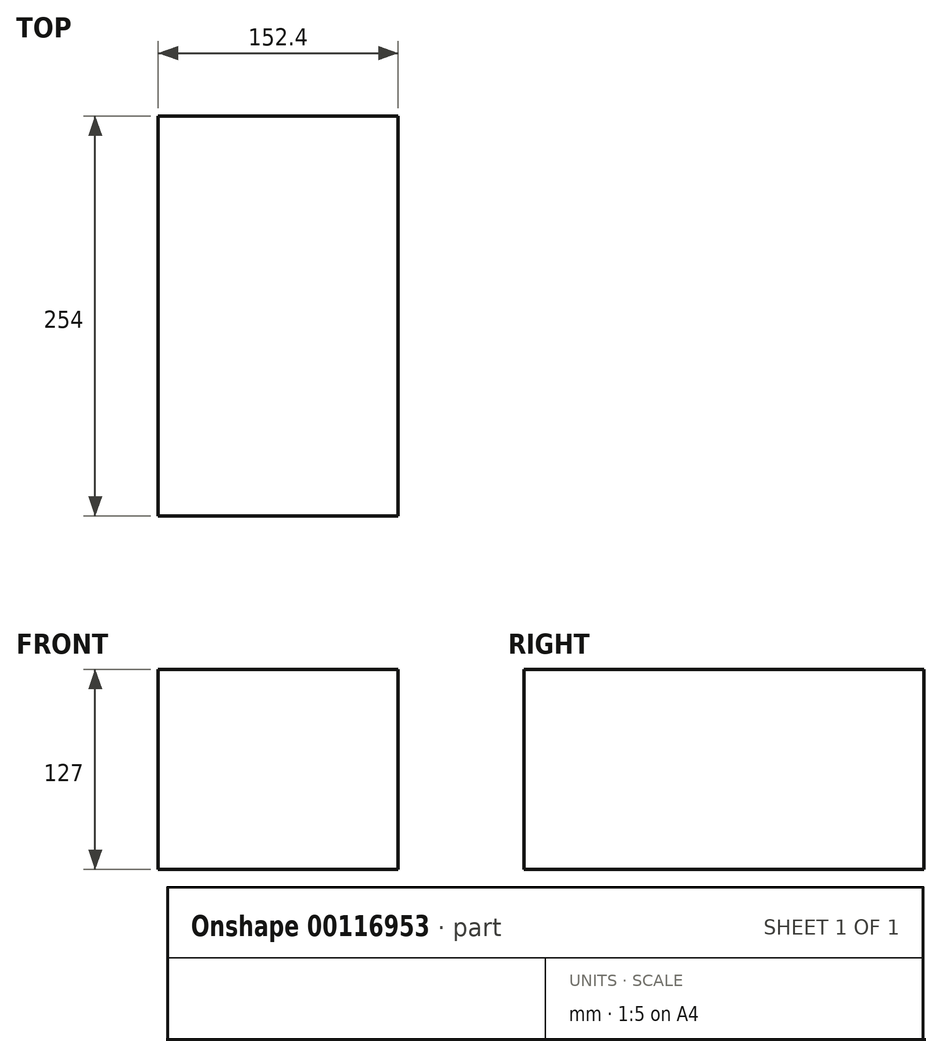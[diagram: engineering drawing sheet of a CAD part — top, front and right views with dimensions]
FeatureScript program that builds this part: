
annotation { "Feature Type Name" : "Feature", "Feature Type Description" : "" }
export const myFeature = defineFeature(function(context is Context, id is Id, definition is map)
    precondition{}
    {
        {
            var Q0;
            Q0=qCreatedBy(makeId("Top.planeOp"),FACE);
            var sketch = newSketch(context, id + "F0", { "sketchPlane" : qUnion([Q0])});
            skLineSegment(sketch, "E0.bottom", {"start": v(-76.2, 127) * mm, "end": v(76.2, 127) * mm});
            skLineSegment(sketch, "E0.top", {"start": v(-76.2, -127) * mm, "end": v(76.2, -127) * mm});
            skLineSegment(sketch, "E0.left", {"start": v(-76.2, 127) * mm, "end": v(-76.2, -127) * mm});
            skLineSegment(sketch, "E0.right", {"start": v(76.2, 127) * mm, "end": v(76.2, -127) * mm});
            skPoint(sketch, "E0.middle", {"position": v(0, 0) * mm});
            skLineSegment(sketch, "E1", {"start": v(0, 0) * mm, "end": v(0, 127) * mm, "construction": true});
            skLineSegment(sketch, "E2", {"start": v(-76.2, 76.2) * mm, "end": v(76.2, 76.2) * mm, "construction": true});
            skLineSegment(sketch, "E3", {"start": v(-63.5, 127) * mm, "end": v(-63.5, 76.2) * mm, "construction": true});
            skLineSegment(sketch, "E4.MirrorCS", {"start": v(63.5, 127) * mm, "end": v(63.5, 76.2) * mm, "construction": true});
            skSolve(sketch);
        }
        {
            var Q0;
            Q0=makeQuery(id+"F0.imprint","IMPRINT",FACE,{"disambiguationData":[TD([[makeQuery(id+"F0.imprint","IMPRINT",EDGE,{"derivedFrom":sQuery(id+"F0.wireOp",EDGE,"E0.bottom")}),-1.0]])]});
            extrude(context, id + "F1", {"entities" : qUnion([Q0]), "oppositeDirection" : true, "depth" : 127 * mm});
        }
    });
